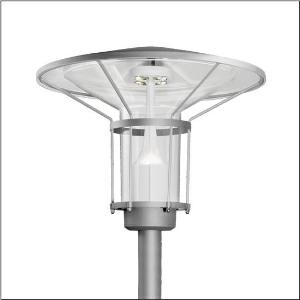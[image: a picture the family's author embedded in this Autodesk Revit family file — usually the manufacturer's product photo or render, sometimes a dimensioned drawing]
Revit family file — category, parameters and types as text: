
# Revit family: laterne_classic_iq___p1_0a_5xa5245nf14hp_be56
name_source: partatom
category: Lighting Fixtures
units: mm (PartAtom-declared; Revit-internal decimal feet)

## family parameters
Cut with Voids When Loaded = No
Host = Face
Light Source = No
Part Type = Normal
Room Calculation Point = No
Round Connector Dimension = Use Diameter
Shared = No

## types (1)
- --- (1 x LED, 3780 lm, 33.6 W, 2700K)
    Apparent Load = 34 VA
    CIE Flux Codes = 31 61 91 96 100
    Color Rendering = 70
    Color Temperature = 2700K
    Default Elevation = 1800 mm
    Description = Lantern Classic iQ, mast luminaire, Module 540 iQ-SR, primary light control with 3 zone facetted reflector, of plastic, silver coated, highly specular, structured, primary optical cover: cover, of PMMA, transparent, light distribution: P1.0a, light emission: direct distribution, primary light characteristic: strongly asymmetric, installation type: post-top, LED, High Power LED, rated luminous flux: 3.780lm, luminous efficacy: 113lm/W, light colour: 727, colour temperature: 2700K, control gear: ECG iQ, control: presetting dimming logarithmic, Street-Remote, Auto-Match, Temp-Guard, Lumen-Switch, Night-Set, Smart-Wire, Light-Fading, Desk-Remote (wireless, voltage-free reading and setting of iQ features in the workshop via application-optimized NFC function/RFID function), optimised constant luminous flux control (CLO 2.0), with terminal, 6-pole, max. 2.5mm², mains connection: 230..240V, AC, 50/60Hz, start of lifetime: 34W, end of service life: 36W, reduction: 15W, luminaire housing, upper part, of glass-fibre reinforced polyester, coated, Siteco® metallic grey (DB 702S), diameter: 750mm, height: 596mm, spigot size: d x l = 76 x 70mm (post-top) | with reducer (optional accessory) 60 x 70mm, post-top mast mounting element, of diecast aluminium, coated, Siteco® metallic grey (DB 702S), Module 540 iQ-SR, traffic white (RAL 9016), equipment: Power, protection rating (complete): IP65, insulation class (complete): insulation class II (safety insulation), certification: CE, ENEC, VDE, packaging unit: 1 piece

Light Distribution: P1.0a
    Height = 596 mm
    Lamp = 1 x LED
    Lamp Light Flux = 3780 lm
    Lamp Power = 33.6 W
    Lamp count = 1
    Length = 750 mm
    Luminous efficacy = 113 lm/W
    Manufacturer = Siteco
    ModVariant = No
    Model = 5XA5245NF14HP
    Number of Poles = 1
    OnlyDefault = Yes
    Power Factor = 1
    Product Name = Laterne Classic iQ | P1.0a
    Product group = mast luminaire | pylon top
    ProductGroupID = 6100
    Protection Class = Protection class II
    Protection Degree = IP 65
    RLX_Detail_Level = 1
    RLX_Emergency_Light_Flux = 0 lm
    RLX_Emergency_Type = 0
    RLX_Emergency_Type_DB = No
    RlxData = <blob elided: 65557 chars, md5=757f53c0>
    Socket = socket
    Standby Power = 0 W
    System Light Flux = 3780 lm
    System Power = 34 W
    Type Comments = factory setting: luminous flux: 100 % | dim-lin: 254 | 695 mA
    Type Image = l_1006052.jpg
    URL = http://relux.com
    VarID = @adj_102773
    Voltage = 0 V
    Weight = 0.00 kg
    Width = 0 mm  [stored 0 ft]

note: [stored X ft] marks values corroborated as IEEE doubles in the binary element streams (Revit-internal decimal feet)

## geometry (parser evidence)
native form markers: Blend x4, Sweep x11
no freeform markers — native parametric forms only
